# Revit family: OASIS TS3P-6032 ABF
name_source: partatom
category: Plumbing Fixtures
revit_build: Autodesk Revit 2017 (Build: 20171027_0315(x64)
units: mm (PartAtom-declared; Revit-internal decimal feet)

## family parameters
Always vertical = Yes
Cut with Voids When Loaded = No
OmniClass Number = 23.45.05.14.21.11
OmniClass Title = Bath/Shower Units
Part Type = Normal
Room Calculation Point = No
Round Connector Dimension = Use Diameter
Shared = No
Work Plane-Based = No

## types (9) — shared parameters
BIM Model By = www.epoch-design.com
Cold Water Connector = Cold Water Connection
Color = <By Category>
Grab Bar Finish = <By Category>
Hot Water Connector = Hot Water Connection
Manufacturer = OASIS
Sanitary Connector = Sanitary Connection
Seat Finish = <By Category>
Stainless steel = <By Category>
Type Comments = TUB/SHOWER
URL = www.oasisbath.com
Waste Connection = No

## per-type parameters (varying)
| type | Bar_Horz_Back_High | Bar_Horz_Back_Low | Bar_Horz_Left | Bar_Horz_Left_ADA10 | Bar_Horz_Right_20" | Bar_Horz_Right_24" | Bar_Vert | Bar_Vert_ANS09 | Model | Seat_Fold | Seat_Remove |
| Base model, 3SF, 3SM, & FH packages | No | No | No | No | No | No | No | No | TS3P-6032 ABF/(3SF,3SM,FH) | No | No |
| BP1-60 package | Yes | No | No | No | Yes | No | No | No | TS3P-6032 ABF/BP1-60 | No | No |
| BP2-60 package | Yes | No | No | No | Yes | No | Yes | No | TS3P-6032 ABF/BP2-60 | No | No |
| 4BAR package | Yes | Yes | Yes | No | Yes | No | No | No | TS3P-6032 ABF/4BAR | No | No |
| 5BAR package | Yes | Yes | Yes | No | Yes | No | Yes | No | TS3P-6032 ABF/5BAR | No | No |
| ADA10-REM package | Yes | Yes | No | Yes | No | Yes | No | No | TS3P-6032 ABF/ADA10-REM | No | Yes |
| ADA10-FLD package | Yes | Yes | No | Yes | No | Yes | No | No | TS3P-6032 ABF/ADA10-FLD | Yes | No |
| ANS17-FLD package | Yes | Yes | No | Yes | No | Yes | No | Yes | TS3P-6032 ABF/ANS17-FLD | Yes | No |
| ANS17-REM package | Yes | Yes | No | Yes | No | Yes | No | Yes | TS3P-6032 ABF/ANS17-REM | No | Yes |

## geometry (parser evidence)
native form markers: Blend x2, Sweep x15
no freeform markers — native parametric forms only
